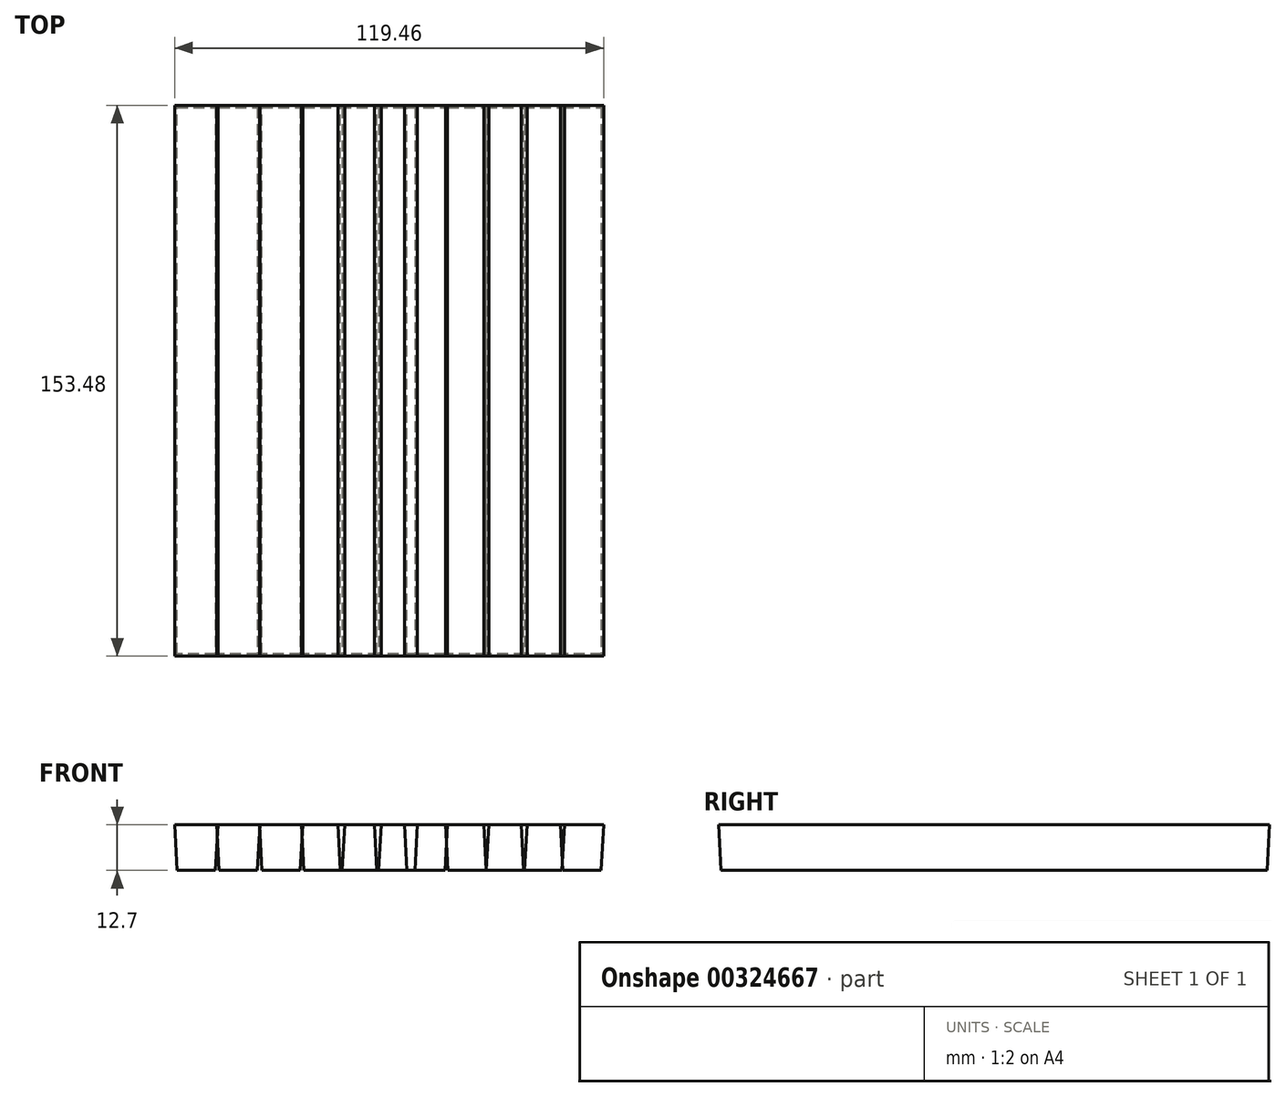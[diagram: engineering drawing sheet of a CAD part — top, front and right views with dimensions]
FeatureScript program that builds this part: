
annotation { "Feature Type Name" : "Feature", "Feature Type Description" : "" }
export const myFeature = defineFeature(function(context is Context, id is Id, definition is map)
    precondition{}
    {
        {
            var Q0;
            Q0=qCreatedBy(makeId("Top.planeOp"),FACE);
            var sketch = newSketch(context, id + "F0", { "sketchPlane" : qUnion([Q0])});
            skLineSegment(sketch, "E0.bottom", {"start": v(-67.5, 75.8) * mm, "end": v(-56.8, 75.8) * mm});
            skLineSegment(sketch, "E0.top", {"start": v(-67.5, -76.35) * mm, "end": v(-56.8, -76.35) * mm});
            skLineSegment(sketch, "E0.left", {"start": v(-67.5, 75.8) * mm, "end": v(-67.5, -76.35) * mm});
            skLineSegment(sketch, "E0.right", {"start": v(-56.8, 75.8) * mm, "end": v(-56.8, -76.35) * mm});
            skSolve(sketch);
        }
        {
            var Q0;
            Q0=makeQuery(id+"F0.imprint","IMPRINT",FACE,{"disambiguationData":[TD([[makeQuery(id+"F0.imprint","IMPRINT",EDGE,{"derivedFrom":sQuery(id+"F0.wireOp",EDGE,"E0.bottom")}),-1.0]])]});
            extrude(context, id + "F1", {"entities" : qUnion([Q0]), "depth" : 12.7 * mm, "hasDraft" : true, "draftAngle" : 3 * degree});
        }
        {
            var Q0;
            Q0=makeQuery(id+"F1.opExtrude","SWEPT_BODY",BODY,{"disambiguationData":[OSD([sQuery(id+"F0.wireOp",EDGE,"E0.bottom"),sQuery(id+"F0.wireOp",EDGE,"E0.top"),sQuery(id+"F0.wireOp",EDGE,"E0.left"),sQuery(id+"F0.wireOp",EDGE,"E0.right")])]});
            transform(context, id + "F2", {"entities" : qUnion([Q0]), "transformType" : TransformType.TRANSLATION_3D, "dx" : 11.68 * mm, "dy" : 0 * mm, "dz" : 0 * mm, "makeCopy" : true});
        }
        {
            var Q0;
            Q0=makeQuery(id+"F1.opExtrude","SWEPT_BODY",BODY,{"disambiguationData":[OSD([sQuery(id+"F0.wireOp",EDGE,"E0.bottom"),sQuery(id+"F0.wireOp",EDGE,"E0.top"),sQuery(id+"F0.wireOp",EDGE,"E0.left"),sQuery(id+"F0.wireOp",EDGE,"E0.right")])]});
            transform(context, id + "F3", {"entities" : qUnion([Q0]), "transformType" : TransformType.TRANSLATION_3D, "dx" : 24.13 * mm, "dy" : 0 * mm, "dz" : 0 * mm, "makeCopy" : true});
        }
        {
            var Q0;
            Q0=makeQuery(id+"F3.opPattern","COPY",BODY,{"derivedFrom":makeQuery(id+"F1.opExtrude","SWEPT_BODY",BODY,{"disambiguationData":[OSD([sQuery(id+"F0.wireOp",EDGE,"E0.bottom"),sQuery(id+"F0.wireOp",EDGE,"E0.top"),sQuery(id+"F0.wireOp",EDGE,"E0.left"),sQuery(id+"F0.wireOp",EDGE,"E0.right")])]}),"instanceName":"1"});
            deleteBodies(context, id + "F4", {"entities" : qUnion([Q0])});
        }
        {
            var Q0;
            Q0=makeQuery(id+"F1.opExtrude","SWEPT_BODY",BODY,{"disambiguationData":[OSD([sQuery(id+"F0.wireOp",EDGE,"E0.bottom"),sQuery(id+"F0.wireOp",EDGE,"E0.top"),sQuery(id+"F0.wireOp",EDGE,"E0.left"),sQuery(id+"F0.wireOp",EDGE,"E0.right")])]});
            transform(context, id + "F5", {"entities" : qUnion([Q0]), "transformType" : TransformType.TRANSLATION_3D, "dx" : 23.62 * mm, "dy" : 0 * mm, "dz" : 0 * mm, "makeCopy" : true});
        }
        {
            var Q0;
            Q0=makeQuery(id+"F5.opPattern","COPY",BODY,{"derivedFrom":makeQuery(id+"F1.opExtrude","SWEPT_BODY",BODY,{"disambiguationData":[OSD([sQuery(id+"F0.wireOp",EDGE,"E0.bottom"),sQuery(id+"F0.wireOp",EDGE,"E0.top"),sQuery(id+"F0.wireOp",EDGE,"E0.left"),sQuery(id+"F0.wireOp",EDGE,"E0.right")])]}),"instanceName":"1"});
            transform(context, id + "F6", {"entities" : qUnion([Q0]), "transformType" : TransformType.TRANSLATION_3D, "dx" : 12.2 * mm, "dy" : 0 * mm, "dz" : 0 * mm, "makeCopy" : true});
        }
        {
            var Q0;
            Q0=makeQuery(id+"F6.opPattern","COPY",BODY,{"derivedFrom":makeQuery(id+"F5.opPattern","COPY",BODY,{"derivedFrom":makeQuery(id+"F1.opExtrude","SWEPT_BODY",BODY,{"disambiguationData":[OSD([sQuery(id+"F0.wireOp",EDGE,"E0.bottom"),sQuery(id+"F0.wireOp",EDGE,"E0.top"),sQuery(id+"F0.wireOp",EDGE,"E0.left"),sQuery(id+"F0.wireOp",EDGE,"E0.right")])]}),"instanceName":"1"}),"instanceName":"1"});
            deleteBodies(context, id + "F7", {"entities" : qUnion([Q0])});
        }
        {
            var Q0;
            Q0=makeQuery(id+"F5.opPattern","COPY",BODY,{"derivedFrom":makeQuery(id+"F1.opExtrude","SWEPT_BODY",BODY,{"disambiguationData":[OSD([sQuery(id+"F0.wireOp",EDGE,"E0.bottom"),sQuery(id+"F0.wireOp",EDGE,"E0.top"),sQuery(id+"F0.wireOp",EDGE,"E0.left"),sQuery(id+"F0.wireOp",EDGE,"E0.right")])]}),"instanceName":"1"});
            transform(context, id + "F8", {"entities" : qUnion([Q0]), "transformType" : TransformType.TRANSLATION_3D, "dx" : 11.68 * mm, "dy" : 0 * mm, "dz" : 0 * mm, "makeCopy" : true});
        }
        {
            var Q0;
            Q0=makeQuery(id+"F8.opPattern","COPY",BODY,{"derivedFrom":makeQuery(id+"F5.opPattern","COPY",BODY,{"derivedFrom":makeQuery(id+"F1.opExtrude","SWEPT_BODY",BODY,{"disambiguationData":[OSD([sQuery(id+"F0.wireOp",EDGE,"E0.bottom"),sQuery(id+"F0.wireOp",EDGE,"E0.top"),sQuery(id+"F0.wireOp",EDGE,"E0.left"),sQuery(id+"F0.wireOp",EDGE,"E0.right")])]}),"instanceName":"1"}),"instanceName":"1"});
            transform(context, id + "F9", {"entities" : qUnion([Q0]), "transformType" : TransformType.TRANSLATION_3D, "dx" : 10.16 * mm, "dy" : 0 * mm, "dz" : 0 * mm, "makeCopy" : true});
        }
        {
            var Q0;
            Q0=makeQuery(id+"F9.opPattern","COPY",BODY,{"derivedFrom":makeQuery(id+"F8.opPattern","COPY",BODY,{"derivedFrom":makeQuery(id+"F5.opPattern","COPY",BODY,{"derivedFrom":makeQuery(id+"F1.opExtrude","SWEPT_BODY",BODY,{"disambiguationData":[OSD([sQuery(id+"F0.wireOp",EDGE,"E0.bottom"),sQuery(id+"F0.wireOp",EDGE,"E0.top"),sQuery(id+"F0.wireOp",EDGE,"E0.left"),sQuery(id+"F0.wireOp",EDGE,"E0.right")])]}),"instanceName":"1"}),"instanceName":"1"}),"instanceName":"1"});
            transform(context, id + "F10", {"entities" : qUnion([Q0]), "transformType" : TransformType.TRANSLATION_3D, "dx" : 10.16 * mm, "dy" : 0 * mm, "dz" : 0 * mm, "makeCopy" : true});
        }
        {
            var Q0;
            Q0=makeQuery(id+"F10.opPattern","COPY",BODY,{"derivedFrom":makeQuery(id+"F9.opPattern","COPY",BODY,{"derivedFrom":makeQuery(id+"F8.opPattern","COPY",BODY,{"derivedFrom":makeQuery(id+"F5.opPattern","COPY",BODY,{"derivedFrom":makeQuery(id+"F1.opExtrude","SWEPT_BODY",BODY,{"disambiguationData":[OSD([sQuery(id+"F0.wireOp",EDGE,"E0.bottom"),sQuery(id+"F0.wireOp",EDGE,"E0.top"),sQuery(id+"F0.wireOp",EDGE,"E0.left"),sQuery(id+"F0.wireOp",EDGE,"E0.right")])]}),"instanceName":"1"}),"instanceName":"1"}),"instanceName":"1"}),"instanceName":"1"});
            transform(context, id + "F11", {"entities" : qUnion([Q0]), "transformType" : TransformType.TRANSLATION_3D, "dx" : 8.38 * mm, "dy" : 0 * mm, "dz" : 0 * mm, "makeCopy" : true});
        }
        {
            var Q0;
            Q0=makeQuery(id+"F11.opPattern","COPY",BODY,{"derivedFrom":makeQuery(id+"F10.opPattern","COPY",BODY,{"derivedFrom":makeQuery(id+"F9.opPattern","COPY",BODY,{"derivedFrom":makeQuery(id+"F8.opPattern","COPY",BODY,{"derivedFrom":makeQuery(id+"F5.opPattern","COPY",BODY,{"derivedFrom":makeQuery(id+"F1.opExtrude","SWEPT_BODY",BODY,{"disambiguationData":[OSD([sQuery(id+"F0.wireOp",EDGE,"E0.bottom"),sQuery(id+"F0.wireOp",EDGE,"E0.top"),sQuery(id+"F0.wireOp",EDGE,"E0.left"),sQuery(id+"F0.wireOp",EDGE,"E0.right")])]}),"instanceName":"1"}),"instanceName":"1"}),"instanceName":"1"}),"instanceName":"1"}),"instanceName":"1"});
            transform(context, id + "F12", {"entities" : qUnion([Q0]), "transformType" : TransformType.TRANSLATION_3D, "dx" : 11.43 * mm, "dy" : 0 * mm, "dz" : 0 * mm, "makeCopy" : true});
        }
        {
            var Q0;
            Q0=makeQuery(id+"F12.opPattern","COPY",BODY,{"derivedFrom":makeQuery(id+"F11.opPattern","COPY",BODY,{"derivedFrom":makeQuery(id+"F10.opPattern","COPY",BODY,{"derivedFrom":makeQuery(id+"F9.opPattern","COPY",BODY,{"derivedFrom":makeQuery(id+"F8.opPattern","COPY",BODY,{"derivedFrom":makeQuery(id+"F5.opPattern","COPY",BODY,{"derivedFrom":makeQuery(id+"F1.opExtrude","SWEPT_BODY",BODY,{"disambiguationData":[OSD([sQuery(id+"F0.wireOp",EDGE,"E0.bottom"),sQuery(id+"F0.wireOp",EDGE,"E0.top"),sQuery(id+"F0.wireOp",EDGE,"E0.left"),sQuery(id+"F0.wireOp",EDGE,"E0.right")])]}),"instanceName":"1"}),"instanceName":"1"}),"instanceName":"1"}),"instanceName":"1"}),"instanceName":"1"}),"instanceName":"1"});
            transform(context, id + "F13", {"entities" : qUnion([Q0]), "transformType" : TransformType.TRANSLATION_3D, "dx" : 10.67 * mm, "dy" : 0 * mm, "dz" : 0 * mm, "makeCopy" : true});
        }
        {
            var Q0;
            Q0=makeQuery(id+"F13.opPattern","COPY",BODY,{"derivedFrom":makeQuery(id+"F12.opPattern","COPY",BODY,{"derivedFrom":makeQuery(id+"F11.opPattern","COPY",BODY,{"derivedFrom":makeQuery(id+"F10.opPattern","COPY",BODY,{"derivedFrom":makeQuery(id+"F9.opPattern","COPY",BODY,{"derivedFrom":makeQuery(id+"F8.opPattern","COPY",BODY,{"derivedFrom":makeQuery(id+"F5.opPattern","COPY",BODY,{"derivedFrom":makeQuery(id+"F1.opExtrude","SWEPT_BODY",BODY,{"disambiguationData":[OSD([sQuery(id+"F0.wireOp",EDGE,"E0.bottom"),sQuery(id+"F0.wireOp",EDGE,"E0.top"),sQuery(id+"F0.wireOp",EDGE,"E0.left"),sQuery(id+"F0.wireOp",EDGE,"E0.right")])]}),"instanceName":"1"}),"instanceName":"1"}),"instanceName":"1"}),"instanceName":"1"}),"instanceName":"1"}),"instanceName":"1"}),"instanceName":"1"});
            transform(context, id + "F14", {"entities" : qUnion([Q0]), "transformType" : TransformType.TRANSLATION_3D, "dx" : 10.4 * mm, "dy" : 0 * mm, "dz" : 0 * mm, "makeCopy" : true});
        }
        {
            var Q0;
            Q0=makeQuery(id+"F14.opPattern","COPY",BODY,{"derivedFrom":makeQuery(id+"F13.opPattern","COPY",BODY,{"derivedFrom":makeQuery(id+"F12.opPattern","COPY",BODY,{"derivedFrom":makeQuery(id+"F11.opPattern","COPY",BODY,{"derivedFrom":makeQuery(id+"F10.opPattern","COPY",BODY,{"derivedFrom":makeQuery(id+"F9.opPattern","COPY",BODY,{"derivedFrom":makeQuery(id+"F8.opPattern","COPY",BODY,{"derivedFrom":makeQuery(id+"F5.opPattern","COPY",BODY,{"derivedFrom":makeQuery(id+"F1.opExtrude","SWEPT_BODY",BODY,{"disambiguationData":[OSD([sQuery(id+"F0.wireOp",EDGE,"E0.bottom"),sQuery(id+"F0.wireOp",EDGE,"E0.top"),sQuery(id+"F0.wireOp",EDGE,"E0.left"),sQuery(id+"F0.wireOp",EDGE,"E0.right")])]}),"instanceName":"1"}),"instanceName":"1"}),"instanceName":"1"}),"instanceName":"1"}),"instanceName":"1"}),"instanceName":"1"}),"instanceName":"1"}),"instanceName":"1"});
            transform(context, id + "F15", {"entities" : qUnion([Q0]), "transformType" : TransformType.TRANSLATION_3D, "dx" : 10.92 * mm, "dy" : 0 * mm, "dz" : 0 * mm, "makeCopy" : true});
        }
    });
